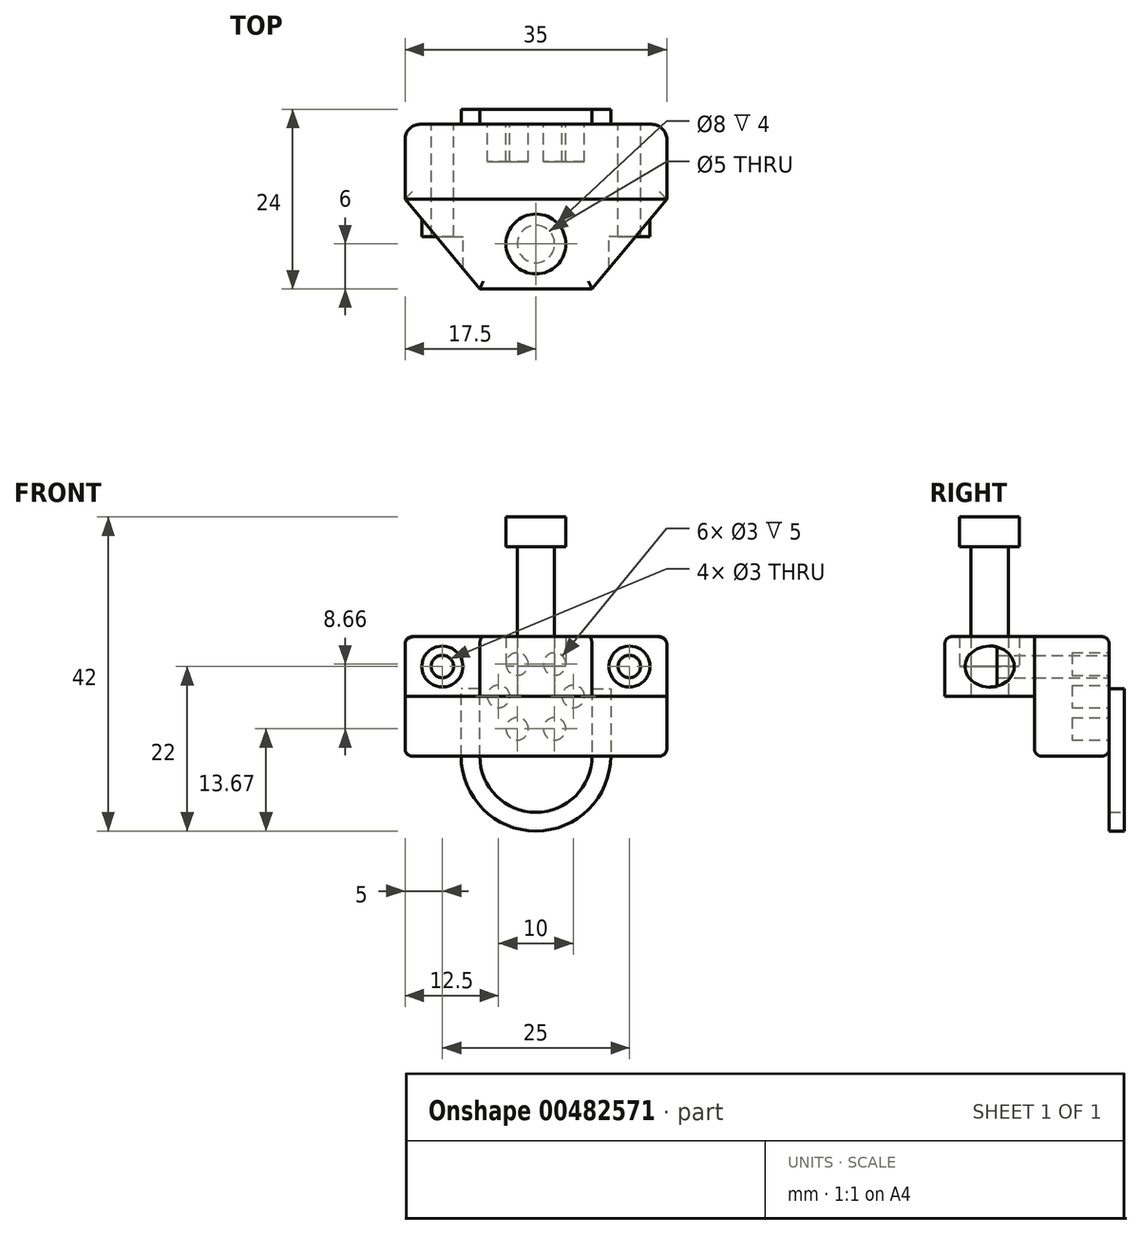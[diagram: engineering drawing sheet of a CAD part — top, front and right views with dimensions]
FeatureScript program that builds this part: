
annotation { "Feature Type Name" : "Feature", "Feature Type Description" : "" }
export const myFeature = defineFeature(function(context is Context, id is Id, definition is map)
    precondition{}
    {
        {
            var Q0;
            Q0=qCreatedBy(makeId("Top.planeOp"),FACE);
            var sketch = newSketch(context, id + "F0", { "sketchPlane" : qUnion([Q0])});
            skLineSegment(sketch, "E0", {"start": v(0, 0) * mm, "end": v(15, 0) * mm});
            skLineSegment(sketch, "E1", {"start": v(15, 0) * mm, "end": v(25, 12) * mm});
            skLineSegment(sketch, "E2", {"start": v(25, 12) * mm, "end": v(-10, 12) * mm});
            skLineSegment(sketch, "E3", {"start": v(-10, 12) * mm, "end": v(0, 0) * mm});
            skLineSegment(sketch, "E4", {"start": v(0, 0) * mm, "end": v(0, 12) * mm, "construction": true});
            skLineSegment(sketch, "E5", {"start": v(15, 0) * mm, "end": v(15, 12) * mm, "construction": true});
            skLineSegment(sketch, "E6", {"start": v(15, 12) * mm, "end": v(25, 12) * mm});
            skLineSegment(sketch, "E7", {"start": v(-10, 12) * mm, "end": v(0, 12) * mm});
            skLineSegment(sketch, "E8", {"start": v(7.5, 12) * mm, "end": v(7.5, 0) * mm, "construction": true});
            skCircle(sketch, "E9", {"center": v(7.5, 6) * mm, "radius": 2.5 * mm});
            skCircle(sketch, "E10", {"center": v(7.5, 6) * mm, "radius": 4 * mm});
            skLineSegment(sketch, "E11", {"start": v(25, 12) * mm, "end": v(25, 20) * mm});
            skLineSegment(sketch, "E12", {"start": v(23, 22) * mm, "end": v(-8, 22) * mm});
            skLineSegment(sketch, "E13", {"start": v(-10, 20) * mm, "end": v(-10, 12) * mm});
            skPoint(sketch, "E14.visualSharp", {"position": v(25, 22) * mm});
            skArc(sketch, "E14.filletArc", {"start": v(25, 20) * mm, "mid": v(24.41, 21.41) * mm, "end": v(23, 22) * mm});
            skPoint(sketch, "E15.visualSharp", {"position": v(-10, 22) * mm});
            skArc(sketch, "E15.filletArc", {"start": v(-8, 22) * mm, "mid": v(-9.41, 21.41) * mm, "end": v(-10, 20) * mm});
            skSolve(sketch);
        }
        {
            var Q0;
            Q0=makeQuery(id+"F0.imprint","IMPRINT",FACE,{"disambiguationData":[TD([[makeQuery(id+"F0.imprint","IMPRINT",EDGE,{"derivedFrom":sQuery(id+"F0.wireOp",EDGE,"E0")}),1.0]])]});
            extrude(context, id + "F1", {"entities" : qUnion([Q0]), "depth" : 8 * mm, "offsetDistance" : 25 * mm});
        }
        {
            var Q0;
            Q0=makeQuery(id+"F0.imprint","IMPRINT",FACE,{"disambiguationData":[TD([[makeQuery(id+"F0.imprint","IMPRINT",EDGE,{"derivedFrom":sQuery(id+"F0.wireOp",EDGE,"E9")}),-1.0]])]});
            extrude(context, id + "F2", {"entities" : qUnion([Q0]), "operationType" : NewBodyOperationType.ADD, "depth" : 4 * mm, "offsetDistance" : 25 * mm});
        }
        {
            var Q0;
            Q0=makeQuery(id+"F0.imprint","IMPRINT",FACE,{"disambiguationData":[TD([[makeQuery(id+"F0.imprint","IMPRINT",EDGE,{"derivedFrom":sQuery(id+"F0.wireOp",EDGE,"E9")}),1.0]])]});
            extrude(context, id + "F3", {"entities" : qUnion([Q0]), "depth" : 20 * mm, "offsetDistance" : 25 * mm});
        }
        {
            var Q0;
            Q0=makeQuery(id+"F3.opExtrude","CAP_FACE",FACE,{"disambiguationData":[OSD([sQuery(id+"F0.wireOp",EDGE,"E9")])],"isStart":false});
            var sketch = newSketch(context, id + "F4", { "sketchPlane" : qUnion([Q0])});
            skCircle(sketch, "E16.0", {"center": v(7.5, 6) * mm, "radius": 4 * mm});
            skSolve(sketch);
        }
        {
            var Q0;
            Q0 = qSketchRegion(id + "F4", true);
            extrude(context, id + "F5", {"entities" : qUnion([Q0]), "operationType" : NewBodyOperationType.ADD, "depth" : 4 * mm, "offsetDistance" : 25 * mm});
        }
        {
            var Q0;
            Q0=makeQuery(id+"F1.opExtrude","SWEPT_FACE",FACE,{"disambiguationData":[OSD([sQuery(id+"F0.wireOp",EDGE,"E2"),sQuery(id+"F0.wireOp",EDGE,"E6"),sQuery(id+"F0.wireOp",EDGE,"E7")])]});
            var sketch = newSketch(context, id + "F6", { "sketchPlane" : qUnion([Q0])});
            skCircle(sketch, "E17", {"center": v(-20, 4) * mm, "radius": 1.5 * mm});
            skLineSegment(sketch, "E18", {"start": v(-20, 4) * mm, "end": v(-20, 8) * mm, "construction": true});
            skLineSegment(sketch, "E19", {"start": v(-20, 4) * mm, "end": v(-20, 0) * mm, "construction": true});
            skPoint(sketch, "E20.endSnap0", {"position": v(-25, 4) * mm});
            skLineSegment(sketch, "E21", {"start": v(-25, 4) * mm, "end": v(-20, 4) * mm, "construction": true});
            skCircle(sketch, "E22", {"center": v(5, 4) * mm, "radius": 1.5 * mm});
            skLineSegment(sketch, "E23", {"start": v(10, 4) * mm, "end": v(5, 4) * mm, "construction": true});
            skLineSegment(sketch, "E24", {"start": v(5, 4) * mm, "end": v(5, 8) * mm, "construction": true});
            skLineSegment(sketch, "E25", {"start": v(5, 4) * mm, "end": v(5, 0) * mm, "construction": true});
            skCircle(sketch, "E26", {"center": v(-20, 4) * mm, "radius": 2.75 * mm});
            skCircle(sketch, "E27", {"center": v(5, 4) * mm, "radius": 2.75 * mm});
            skSolve(sketch);
        }
        {
            var Q0;
            Q0=makeQuery(id+"F6.imprint","IMPRINT",FACE,{"disambiguationData":[TD([[makeQuery(id+"F6.imprint","IMPRINT",EDGE,{"derivedFrom":sQuery(id+"F6.wireOp",EDGE,"E17")}),1.0]])]});
            var Q1;
            Q1=makeQuery(id+"F6.imprint","IMPRINT",FACE,{"disambiguationData":[TD([[makeQuery(id+"F6.imprint","IMPRINT",EDGE,{"derivedFrom":sQuery(id+"F6.wireOp",EDGE,"E22")}),1.0]])]});
            extrude(context, id + "F7", {"entities" : qUnion([Q0, Q1]), "operationType" : NewBodyOperationType.REMOVE, "endBound" : BoundingType.THROUGH_ALL, "oppositeDirection" : true, "depth" : 25 * mm, "offsetDistance" : 25 * mm});
        }
        {
            var Q0;
            Q0=makeQuery(id+"F6.imprint","IMPRINT",FACE,{"disambiguationData":[TD([[makeQuery(id+"F6.imprint","IMPRINT",EDGE,{"derivedFrom":sQuery(id+"F6.wireOp",EDGE,"E17")}),-1.0]])]});
            var Q1;
            Q1=makeQuery(id+"F6.imprint","IMPRINT",FACE,{"disambiguationData":[TD([[makeQuery(id+"F6.imprint","IMPRINT",EDGE,{"derivedFrom":sQuery(id+"F6.wireOp",EDGE,"E22")}),-1.0]])]});
            extrude(context, id + "F8", {"entities" : qUnion([Q0, Q1]), "operationType" : NewBodyOperationType.ADD, "oppositeDirection" : true, "depth" : 5 * mm, "offsetDistance" : 25 * mm});
        }
        {
            var Q0;
            Q0=makeQuery(id+"F8.opExtrude","CAP_FACE",FACE,{"disambiguationData":[OSD([sQuery(id+"F6.wireOp",EDGE,"E17"),sQuery(id+"F6.wireOp",EDGE,"E26")])],"isStart":false});
            var sketch = newSketch(context, id + "F9", { "sketchPlane" : qUnion([Q0])});
            skCircle(sketch, "E28.0", {"center": v(20, 4) * mm, "radius": 2.75 * mm});
            skCircle(sketch, "E29.0", {"center": v(-5, 4) * mm, "radius": 2.75 * mm});
            skSolve(sketch);
        }
        {
            var Q0;
            Q0 = qSketchRegion(id + "F9", true);
            extrude(context, id + "F10", {"entities" : qUnion([Q0]), "operationType" : NewBodyOperationType.REMOVE, "endBound" : BoundingType.THROUGH_ALL, "depth" : 25 * mm, "offsetDistance" : 25 * mm});
        }
        {
            var Q0;
            Q0=makeQuery(id+"F1.opExtrude","CAP_EDGE",EDGE,{"disambiguationData":[OSD([sQuery(id+"F0.wireOp",EDGE,"E3")])],"isStart":false});
            var Q1;
            Q1=makeQuery(id+"F1.opExtrude","CAP_EDGE",EDGE,{"disambiguationData":[OSD([sQuery(id+"F0.wireOp",EDGE,"E0")])],"isStart":false});
            var Q2;
            Q2=makeQuery(id+"F1.opExtrude","CAP_EDGE",EDGE,{"disambiguationData":[OSD([sQuery(id+"F0.wireOp",EDGE,"E1")])],"isStart":false});
            fillet(context, id + "F11", {"entities" : qUnion([Q0, Q1, Q2]), "radius" : 1 * mm, "tangentPropagation" : true, "allowEdgeOverflow" : false});
        }
        {
            var Q0;
            Q0=makeQuery(id+"F0.imprint","IMPRINT",FACE,{"disambiguationData":[TD([[makeQuery(id+"F0.imprint","IMPRINT",EDGE,{"derivedFrom":sQuery(id+"F0.wireOp",EDGE,"E2")}),-1.0]])]});
            extrude(context, id + "F12", {"entities" : qUnion([Q0]), "endBound" : BoundingType.SYMMETRIC, "depth" : 16 * mm, "offsetDistance" : 25 * mm});
        }
        {
            var Q0;
            Q0=makeQuery(id+"F12.opExtrude","SWEPT_FACE",FACE,{"disambiguationData":[OSD([sQuery(id+"F0.wireOp",EDGE,"E12")])]});
            var sketch = newSketch(context, id + "F13", { "sketchPlane" : qUnion([Q0])});
            skCircle(sketch, "E30.0", {"center": v(-20, 4) * mm, "radius": 1.5 * mm});
            skCircle(sketch, "E31.0", {"center": v(5, 4) * mm, "radius": 1.5 * mm});
            skLineSegment(sketch, "E32", {"start": v(-23, 0) * mm, "end": v(8, 0) * mm, "construction": true});
            skPoint(sketch, "E33", {"position": v(-7.5, 0) * mm});
            skCircle(sketch, "E34", {"center": v(-12.5, 0) * mm, "radius": 1.5 * mm});
            skLineSegment(sketch, "E35", {"start": v(-12.5, 0) * mm, "end": v(-7.5, 0) * mm});
            skCircle(sketch, "E36.1.0", {"center": v(-10, -4.33) * mm, "radius": 1.5 * mm});
            skCircle(sketch, "E36.2.0", {"center": v(-5, -4.33) * mm, "radius": 1.5 * mm});
            skCircle(sketch, "E36.3.0", {"center": v(-2.5, 0) * mm, "radius": 1.5 * mm});
            skCircle(sketch, "E36.4.0", {"center": v(-5, 4.33) * mm, "radius": 1.5 * mm});
            skCircle(sketch, "E36.5.0", {"center": v(-10, 4.33) * mm, "radius": 1.5 * mm});
            skLineSegment(sketch, "E37", {"start": v(-17.5, 0) * mm, "end": v(-15, 0) * mm});
            skLineSegment(sketch, "E38", {"start": v(-15, 0) * mm, "end": v(-15, 1) * mm, "construction": true});
            skLineSegment(sketch, "E39", {"start": v(-15, 1) * mm, "end": v(-17.5, 1) * mm});
            skLineSegment(sketch, "E40", {"start": v(-17.5, 1) * mm, "end": v(-17.5, 0) * mm, "construction": true});
            skLineSegment(sketch, "E41", {"start": v(0, 0) * mm, "end": v(0, 1) * mm});
            skLineSegment(sketch, "E42", {"start": v(0, 1) * mm, "end": v(2.5, 1) * mm});
            skLineSegment(sketch, "E43", {"start": v(2.5, 1) * mm, "end": v(2.5, 0) * mm});
            skLineSegment(sketch, "E44", {"start": v(-16.25, 1) * mm, "end": v(-16.25, -8) * mm});
            skLineSegment(sketch, "E45", {"start": v(1.25, 1) * mm, "end": v(1.25, -8) * mm});
            skArc(sketch, "E46", {"start": v(-16.25, -8) * mm, "mid": v(-7.5, -16.75) * mm, "end": v(1.25, -8) * mm});
            skSolve(sketch);
        }
        {
            var Q0;
            Q0=makeQuery(id+"F13.imprint","IMPRINT",FACE,{"disambiguationData":[TD([[makeQuery(id+"F13.imprint","IMPRINT",EDGE,{"derivedFrom":sQuery(id+"F13.wireOp",EDGE,"E30.0")}),1.0]])]});
            var Q1;
            Q1=makeQuery(id+"F13.imprint","IMPRINT",FACE,{"disambiguationData":[TD([[makeQuery(id+"F13.imprint","IMPRINT",EDGE,{"derivedFrom":sQuery(id+"F13.wireOp",EDGE,"E31.0")}),1.0]])]});
            extrude(context, id + "F14", {"entities" : qUnion([Q0, Q1]), "operationType" : NewBodyOperationType.REMOVE, "endBound" : BoundingType.THROUGH_ALL, "oppositeDirection" : true, "depth" : 25 * mm, "offsetDistance" : 25 * mm});
        }
        {
            var Q0;
            Q0=makeQuery(id+"F13.imprint","IMPRINT",FACE,{"disambiguationData":[TD([[makeQuery(id+"F13.imprint","IMPRINT",EDGE,{"derivedFrom":sQuery(id+"F13.wireOp",EDGE,"E36.5.0")}),1.0]])]});
            var Q1;
            Q1=makeQuery(id+"F13.imprint","IMPRINT",FACE,{"disambiguationData":[TD([[makeQuery(id+"F13.imprint","IMPRINT",EDGE,{"derivedFrom":sQuery(id+"F13.wireOp",EDGE,"E34")}),1.0]])]});
            var Q2;
            Q2=makeQuery(id+"F13.imprint","IMPRINT",FACE,{"disambiguationData":[TD([[makeQuery(id+"F13.imprint","IMPRINT",EDGE,{"derivedFrom":sQuery(id+"F13.wireOp",EDGE,"E36.4.0")}),1.0]])]});
            var Q3;
            Q3=makeQuery(id+"F13.imprint","IMPRINT",FACE,{"disambiguationData":[TD([[makeQuery(id+"F13.imprint","IMPRINT",EDGE,{"derivedFrom":sQuery(id+"F13.wireOp",EDGE,"E36.1.0")}),1.0]])]});
            var Q4;
            Q4=makeQuery(id+"F13.imprint","IMPRINT",FACE,{"disambiguationData":[TD([[makeQuery(id+"F13.imprint","IMPRINT",EDGE,{"derivedFrom":sQuery(id+"F13.wireOp",EDGE,"E36.2.0")}),1.0]])]});
            var Q5;
            Q5=makeQuery(id+"F13.imprint","IMPRINT",FACE,{"disambiguationData":[TD([[makeQuery(id+"F13.imprint","IMPRINT",EDGE,{"derivedFrom":sQuery(id+"F13.wireOp",EDGE,"E36.3.0")}),1.0]])]});
            extrude(context, id + "F15", {"entities" : qUnion([Q0, Q1, Q2, Q3, Q4, Q5]), "operationType" : NewBodyOperationType.REMOVE, "oppositeDirection" : true, "depth" : 5 * mm, "offsetDistance" : 25 * mm});
        }
        {
            var Q0;
            Q0=makeQuery(id+"F12.opExtrude","CAP_EDGE",EDGE,{"disambiguationData":[OSD([sQuery(id+"F0.wireOp",EDGE,"E11")])],"isStart":false});
            var Q1;
            Q1=makeQuery(id+"F12.opExtrude","CAP_EDGE",EDGE,{"disambiguationData":[OSD([sQuery(id+"F0.wireOp",EDGE,"E11")])],"isStart":true});
            var Q2;
            Q2=makeQuery(id+"F12.opExtrude","CAP_EDGE",EDGE,{"disambiguationData":[OSD([sQuery(id+"F0.wireOp",EDGE,"E2"),sQuery(id+"F0.wireOp",EDGE,"E6"),sQuery(id+"F0.wireOp",EDGE,"E7")])],"isStart":true});
            fillet(context, id + "F16", {"entities" : qUnion([Q0, Q1, Q2]), "radius" : 1 * mm, "tangentPropagation" : true, "allowEdgeOverflow" : false});
        }
        {
            var Q0;
            Q0=sQuery(id+"F13.wireOp",EDGE,"E39");
            extrude(context, id + "F17", {"bodyType" : ToolBodyType.SURFACE, "surfaceEntities" : qUnion([Q0]), "depth" : 2 * mm, "offsetDistance" : 25 * mm});
        }
        {
            var Q0;
            Q0=makeQuery(id+"F17.opExtrude","SWEPT_FACE",FACE,{"disambiguationData":[OSD([sQuery(id+"F13.wireOp",EDGE,"E39")])]});
            var Q1;
            Q1=sQuery(id+"F13.wireOp",EDGE,"E44");
            var Q2;
            Q2=sQuery(id+"F13.wireOp",EDGE,"E46");
            var Q3;
            Q3=sQuery(id+"F13.wireOp",EDGE,"E45");
            sweep(context, id + "F18", {"profiles" : qUnion([Q0]), "path" : qUnion([Q1, Q2, Q3])});
        }
    });
